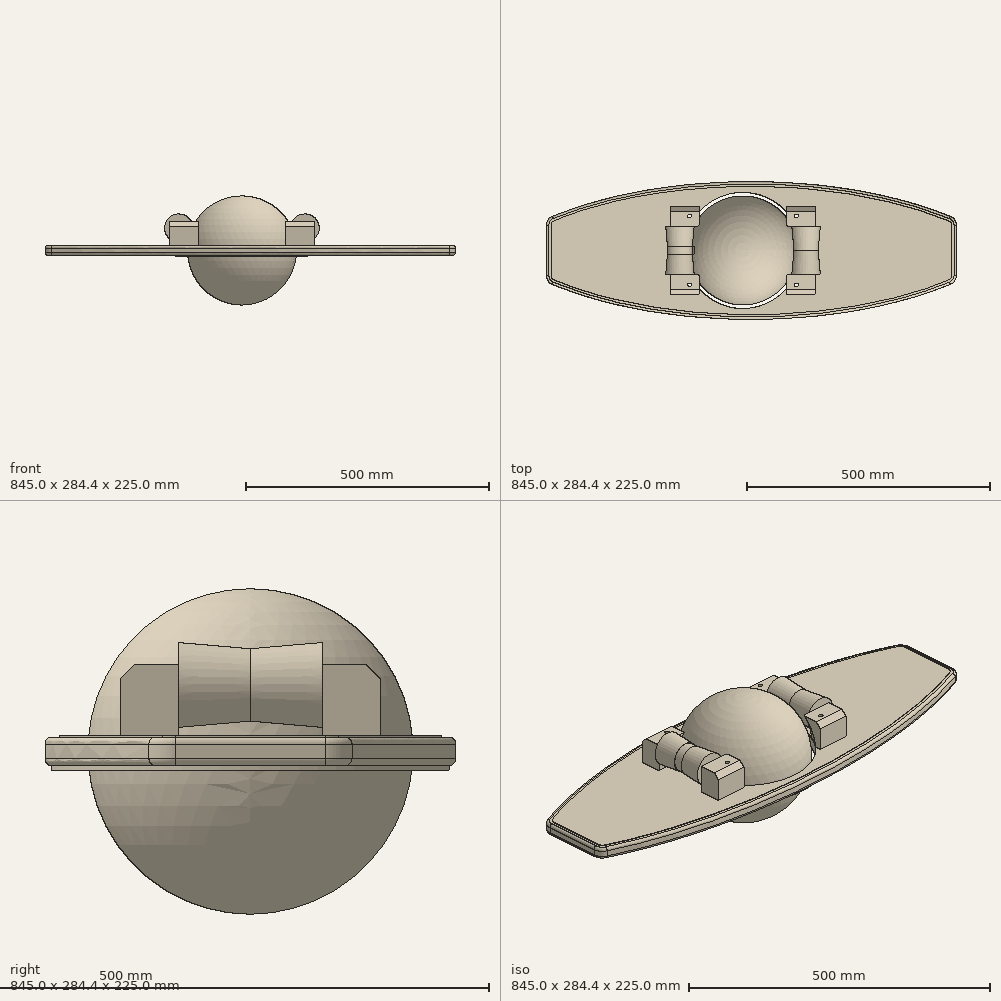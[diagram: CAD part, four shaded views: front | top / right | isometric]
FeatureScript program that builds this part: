
annotation { "Feature Type Name" : "Feature", "Feature Type Description" : "" }
export const myFeature = defineFeature(function(context is Context, id is Id, definition is map)
    precondition{}
    {
        {
            var Q0;
            Q0=qCreatedBy(makeId("Top.planeOp"),FACE);
            var sketch = newSketch(context, id + "F0", { "sketchPlane" : qUnion([Q0])});
            skLineSegment(sketch, "E0.bottom", {"start": v(440, 127.5) * mm, "end": v(-440, 127.5) * mm, "construction": true});
            skLineSegment(sketch, "E0.top", {"start": v(440, -127.5) * mm, "end": v(-440, -127.5) * mm, "construction": true});
            skLineSegment(sketch, "E0.left", {"start": v(440, 127.5) * mm, "end": v(440, -127.5) * mm, "construction": true});
            skLineSegment(sketch, "E0.right", {"start": v(-405, 51.76) * mm, "end": v(-405, -51.76) * mm});
            skPoint(sketch, "E0.middle", {"position": v(0, 0) * mm});
            skLineSegment(sketch, "E1", {"start": v(-441.65, 0) * mm, "end": v(552.98, 0) * mm, "construction": true});
            skPoint(sketch, "E1.startSnap0", {"position": v(-405, 0) * mm});
            skLineSegment(sketch, "E2", {"start": v(0, 265.18) * mm, "end": v(0, -302.26) * mm, "construction": true});
            skFitSpline(sketch, "E3", {"points": [v(-405, 65) * mm, v(440, 65) * mm], "startDerivative": vector(703.3, 306.5) * mm, "endDerivative": vector(719, -310.94) * mm});
            skFitSpline(sketch, "E4.MirrorCS", {"points": [v(-405, -65) * mm, v(440, -65) * mm], "startDerivative": vector(703.3, -306.5) * mm, "endDerivative": vector(719, 310.94) * mm});
            skLineSegment(sketch, "E5", {"start": v(440, -51.72) * mm, "end": v(440, 51.72) * mm});
            skPoint(sketch, "E6.newPointB", {"position": v(-405, 127.5) * mm});
            skArc(sketch, "E6.filletArc", {"start": v(-392.63, 70.25) * mm, "mid": v(-401.62, 62.88) * mm, "end": v(-405, 51.76) * mm});
            skPoint(sketch, "E7.newPointB", {"position": v(-405, -127.5) * mm});
            skArc(sketch, "E7.filletArc", {"start": v(-405, -51.76) * mm, "mid": v(-401.62, -62.88) * mm, "end": v(-392.63, -70.25) * mm});
            skArc(sketch, "E8.filletArc", {"start": v(440, 51.72) * mm, "mid": v(436.6, 62.86) * mm, "end": v(427.59, 70.23) * mm});
            skArc(sketch, "E9.filletArc", {"start": v(427.59, -70.23) * mm, "mid": v(436.6, -62.86) * mm, "end": v(440, -51.72) * mm});
            skSolve(sketch);
        }
        {
            var Q0;
            Q0 = qSketchRegion(id + "F0", true);
            extrude(context, id + "F1", {"entities" : qUnion([Q0]), "depth" : 10 * mm, "offsetDistance" : 25 * mm, "hasSecondDirection" : true, "secondDirectionOppositeDirection" : true, "secondDirectionDepth" : 10 * mm});
        }
        {
            var Q0;
            Q0=makeQuery(id+"F1.opExtrude","CAP_FACE",FACE,{"disambiguationData":[OSD([sQuery(id+"F0.wireOp",EDGE,"E0.right"),sQuery(id+"F0.wireOp",EDGE,"E3"),sQuery(id+"F0.wireOp",EDGE,"E4.MirrorCS"),sQuery(id+"F0.wireOp",EDGE,"E5"),sQuery(id+"F0.wireOp",EDGE,"E6.filletArc"),sQuery(id+"F0.wireOp",EDGE,"E7.filletArc"),sQuery(id+"F0.wireOp",EDGE,"E8.filletArc"),sQuery(id+"F0.wireOp",EDGE,"E9.filletArc")])],"isStart":false});
            var sketch = newSketch(context, id + "F2", { "sketchPlane" : qUnion([Q0])});
            skLineSegment(sketch, "E10", {"start": v(199.73, 164.42) * mm, "end": v(199.73, -153.38) * mm, "construction": true});
            skLineSegment(sketch, "E11.MirrorCS", {"start": v(-199.73, 164.42) * mm, "end": v(-199.73, -153.38) * mm, "construction": true});
            skEllipse(sketch, "E12", {"center": v(0, 0) * mm, "majorRadius": 262.5 * mm, "minorRadius": 137.5 * mm, "majorAxis": v(1, 0)});
            skSolve(sketch);
        }
        {
            var Q0;
            Q0=qCreatedBy(makeId("Front.planeOp"),FACE);
            var sketch = newSketch(context, id + "F3", { "sketchPlane" : qUnion([Q0])});
            skLineSegment(sketch, "E13", {"start": v(0, 153.53) * mm, "end": v(0, -137.68) * mm, "construction": true});
            skArc(sketch, "E14", {"start": v(0, -120) * mm, "mid": v(120, 0) * mm, "end": v(0, 120) * mm});
            skPoint(sketch, "E15", {"position": v(0, 120) * mm});
            skPoint(sketch, "E16", {"position": v(0, -120) * mm});
            skLineSegment(sketch, "E17", {"start": v(0, 120) * mm, "end": v(0, -120) * mm});
            skSolve(sketch);
        }
        {
            var Q0;
            Q0=makeQuery(id+"F1.opExtrude","CAP_FACE",FACE,{"disambiguationData":[OSD([sQuery(id+"F0.wireOp",EDGE,"E0.right"),sQuery(id+"F0.wireOp",EDGE,"E3"),sQuery(id+"F0.wireOp",EDGE,"E4.MirrorCS"),sQuery(id+"F0.wireOp",EDGE,"E5"),sQuery(id+"F0.wireOp",EDGE,"E6.filletArc"),sQuery(id+"F0.wireOp",EDGE,"E7.filletArc"),sQuery(id+"F0.wireOp",EDGE,"E8.filletArc"),sQuery(id+"F0.wireOp",EDGE,"E9.filletArc")])],"isStart":false});
            var sketch = newSketch(context, id + "F4", { "sketchPlane" : qUnion([Q0])});
            skCircle(sketch, "E18", {"center": v(0, 0) * mm, "radius": 120 * mm});
            skLineSegment(sketch, "E19", {"start": v(-413.94, 0) * mm, "end": v(421.24, 0) * mm, "construction": true});
            skPoint(sketch, "E19.endSnap0", {"position": v(-405, 0) * mm});
            skLineSegment(sketch, "E20", {"start": v(430.63, 50) * mm, "end": v(-484.6, 50) * mm, "construction": true});
            skLineSegment(sketch, "E21.bottom", {"start": v(180, 90) * mm, "end": v(90, 90) * mm});
            skLineSegment(sketch, "E21.top", {"start": v(180, 50) * mm, "end": v(90, 50) * mm});
            skLineSegment(sketch, "E21.left", {"start": v(180, 90) * mm, "end": v(180, 50) * mm});
            skLineSegment(sketch, "E21.right", {"start": v(90, 90) * mm, "end": v(90, 50) * mm});
            skLineSegment(sketch, "E22.MirrorCS", {"start": v(90, -90) * mm, "end": v(90, -50) * mm});
            skLineSegment(sketch, "E23.MirrorCS", {"start": v(180, -90) * mm, "end": v(90, -90) * mm});
            skLineSegment(sketch, "E24.MirrorCS", {"start": v(180, -90) * mm, "end": v(180, -50) * mm});
            skLineSegment(sketch, "E25.MirrorCS", {"start": v(180, -50) * mm, "end": v(90, -50) * mm});
            skLineSegment(sketch, "E26", {"start": v(0, 157.92) * mm, "end": v(0, -165.21) * mm, "construction": true});
            skLineSegment(sketch, "E27.MirrorCS", {"start": v(-90, -90) * mm, "end": v(-90, -50) * mm});
            skLineSegment(sketch, "E28.MirrorCS", {"start": v(-90, 90) * mm, "end": v(-90, 50) * mm});
            skLineSegment(sketch, "E29.MirrorCS", {"start": v(-180, 90) * mm, "end": v(-90, 90) * mm});
            skLineSegment(sketch, "E30.MirrorCS", {"start": v(-180, 90) * mm, "end": v(-180, 50) * mm});
            skLineSegment(sketch, "E31.MirrorCS", {"start": v(-180, -90) * mm, "end": v(-180, -50) * mm});
            skLineSegment(sketch, "E32.MirrorCS", {"start": v(-180, -90) * mm, "end": v(-90, -90) * mm});
            skLineSegment(sketch, "E33.MirrorCS", {"start": v(-180, -50) * mm, "end": v(-90, -50) * mm});
            skLineSegment(sketch, "E34.MirrorCS", {"start": v(-180, 50) * mm, "end": v(-90, 50) * mm});
            skSolve(sketch);
        }
        {
            var Q0;
            {var subQ4=sQuery(id+"F4.wireOp",EDGE,"E23.MirrorCS");Q0=makeQuery(id+"F4.imprint","IMPRINT",FACE,{"disambiguationData":[TD([[makeQuery(id+"F4.imprint","IMPRINT",EDGE,{"derivedFrom":subQ4}),-1.0]])]});}
            var Q1;
            {var subQ0=sQuery(id+"F4.wireOp",EDGE,"E25.MirrorCS");var subQ1=sQuery(id+"F4.wireOp",EDGE,"E22.MirrorCS");var subQ2=makeQuery(id+"F4.imprint","INTERSECT",VERTEX,{"derivedFrom":[subQ1,subQ0]});Q1=makeQuery(id+"F4.imprint","IMPRINT",FACE,{"disambiguationData":[TD([[makeQuery(id+"F4.imprint","IMPRINT",EDGE,{"disambiguationData":[TD([[subQ2,1.0]])],"derivedFrom":subQ1}),-1.0]])]});}
            extrude(context, id + "F5", {"entities" : qUnion([Q0, Q1]), "depth" : 50 * mm, "offsetDistance" : 25 * mm});
        }
        {
            var Q0;
            Q0 = qSketchRegion(id + "F3", true);
            var Q1;
            Q1=sQuery(id+"F3.wireOp",EDGE,"E13");
            revolve(context, id + "F6", {"operationType" : NewBodyOperationType.REMOVE, "entities" : qUnion([Q0]), "axis" : qUnion([Q1]), "revolveType" : RevolveType.FULL, "oppositeDirection" : true});
        }
        {
            var Q0;
            Q0=qCreatedBy(makeId("Front.planeOp"),FACE);
            var sketch = newSketch(context, id + "F7", { "sketchPlane" : qUnion([Q0])});
            skArc(sketch, "E35", {"start": v(0, -112.5) * mm, "mid": v(112.5, 0) * mm, "end": v(0, 112.5) * mm});
            skLineSegment(sketch, "E36", {"start": v(0, 156.26) * mm, "end": v(0, -184.84) * mm});
            skSolve(sketch);
        }
        {
            var Q0;
            Q0 = qSketchRegion(id + "F7", true);
            var Q1;
            Q1=sQuery(id+"F7.wireOp",EDGE,"E36");
            revolve(context, id + "F8", {"entities" : qUnion([Q0]), "axis" : qUnion([Q1]), "revolveType" : RevolveType.FULL});
        }
        {
            var Q0;
            Q0=qCreatedBy(makeId("Front.planeOp"),FACE);
            var sketch = newSketch(context, id + "F9", { "sketchPlane" : qUnion([Q0])});
            skCircle(sketch, "E37", {"center": v(130, 46) * mm, "radius": 25 * mm});
            skCircle(sketch, "E38", {"center": v(130, 46) * mm, "radius": 6 * mm});
            skSolve(sketch);
        }
        {
            var Q0;
            Q0=makeQuery(id+"F5.opExtrude","SWEPT_FACE",FACE,{"disambiguationData":[OSD([sQuery(id+"F4.wireOp",EDGE,"E25.MirrorCS")])]});
            var sketch = newSketch(context, id + "F10", { "sketchPlane" : qUnion([Q0])});
            skCircle(sketch, "E39.0", {"center": v(-130, 46) * mm, "radius": 6 * mm});
            skSolve(sketch);
        }
        {
            var Q0;
            Q0 = qSketchRegion(id + "F10", true);
            extrude(context, id + "F11", {"entities" : qUnion([Q0]), "operationType" : NewBodyOperationType.REMOVE, "oppositeDirection" : true, "depth" : 20 * mm, "offsetDistance" : 25 * mm});
        }
        {
            var Q0;
            Q0=makeQuery(id+"F5.opExtrude","SWEPT_FACE",FACE,{"disambiguationData":[OSD([sQuery(id+"F4.wireOp",EDGE,"E25.MirrorCS")])]});
            var sketch = newSketch(context, id + "F12", { "sketchPlane" : qUnion([Q0])});
            skLineSegment(sketch, "E40.bottom", {"start": v(-180, 60) * mm, "end": v(-150, 60) * mm});
            skLineSegment(sketch, "E40.top", {"start": v(-180, 10) * mm, "end": v(-150, 10) * mm});
            skLineSegment(sketch, "E40.left", {"start": v(-180, 60) * mm, "end": v(-180, 10) * mm});
            skLineSegment(sketch, "E40.right", {"start": v(-150, 60) * mm, "end": v(-150, 10) * mm});
            skSolve(sketch);
        }
        {
            var Q0;
            Q0 = qSketchRegion(id + "F12", true);
            extrude(context, id + "F13", {"entities" : qUnion([Q0]), "operationType" : NewBodyOperationType.REMOVE, "endBound" : BoundingType.THROUGH_ALL, "oppositeDirection" : true, "depth" : 25 * mm, "offsetDistance" : 25 * mm});
        }
        {
            var Q0;
            Q0=makeQuery(id+"F9.imprint","IMPRINT",FACE,{"disambiguationData":[TD([[makeQuery(id+"F9.imprint","IMPRINT",EDGE,{"derivedFrom":sQuery(id+"F9.wireOp",EDGE,"E37")}),1.0]])]});
            extrude(context, id + "F14", {"entities" : qUnion([Q0]), "depth" : 49.5 * mm, "offsetDistance" : 25 * mm, "hasDraft" : true, "draftAngle" : 5 * degree, "hasSecondDirection" : true, "secondDirectionOppositeDirection" : true, "secondDirectionDepth" : 49.5 * mm, "hasSecondDirectionDraft" : true, "secondDirectionDraftAngle" : 5 * degree});
        }
        {
            var Q0;
            Q0=makeQuery(id+"F14.opExtrude","CAP_FACE",FACE,{"disambiguationData":[OSD([sQuery(id+"F9.wireOp",EDGE,"E37"),sQuery(id+"F9.wireOp",EDGE,"E38")])],"isStart":true});
            var sketch = newSketch(context, id + "F15", { "sketchPlane" : qUnion([Q0])});
            skCircle(sketch, "E41", {"center": v(-130, 46) * mm, "radius": 6 * mm});
            skSolve(sketch);
        }
        {
            var Q0;
            Q0 = qSketchRegion(id + "F15", true);
            var Q1;
            Q1=makeQuery(id+"F14.opExtrude","CAP_FACE",FACE,{"disambiguationData":[OSD([sQuery(id+"F9.wireOp",EDGE,"E37"),sQuery(id+"F9.wireOp",EDGE,"E38")])],"isStart":false});
            extrude(context, id + "F16", {"entities" : qUnion([Q0]), "operationType" : NewBodyOperationType.REMOVE, "endBound" : BoundingType.UP_TO_SURFACE, "oppositeDirection" : true, "depth" : 25 * mm, "endBoundEntityFace" : qUnion([Q1]), "offsetDistance" : 25 * mm});
        }
        {
            var Q0;
            Q0=qCreatedBy(makeId("Front.planeOp"),FACE);
            var sketch = newSketch(context, id + "F17", { "sketchPlane" : qUnion([Q0])});
            skCircle(sketch, "E42.0", {"center": v(130, 46) * mm, "radius": 6 * mm});
            skSolve(sketch);
        }
        {
            var Q0;
            Q0=makeQuery(id+"F5.opExtrude","CAP_FACE",FACE,{"disambiguationData":[OSD([sQuery(id+"F4.wireOp",EDGE,"E22.MirrorCS"),sQuery(id+"F4.wireOp",EDGE,"E23.MirrorCS"),sQuery(id+"F4.wireOp",EDGE,"E24.MirrorCS"),sQuery(id+"F4.wireOp",EDGE,"E25.MirrorCS")])],"isStart":false});
            var sketch = newSketch(context, id + "F18", { "sketchPlane" : qUnion([Q0])});
            skCircle(sketch, "E43", {"center": v(110, -70.98) * mm, "radius": 4 * mm});
            skPoint(sketch, "E43.centerSnap0", {"position": v(90, -70.98) * mm});
            skSolve(sketch);
        }
        {
            var Q0;
            Q0=makeQuery(id+"F18.imprint","IMPRINT",FACE,{"disambiguationData":[TD([[makeQuery(id+"F18.imprint","IMPRINT",EDGE,{"derivedFrom":sQuery(id+"F18.wireOp",EDGE,"E43")}),1.0]])]});
            extrude(context, id + "F19", {"entities" : qUnion([Q0]), "operationType" : NewBodyOperationType.REMOVE, "endBound" : BoundingType.THROUGH_ALL, "oppositeDirection" : true, "depth" : 25 * mm, "offsetDistance" : 25 * mm});
        }
        {
            var Q0;
            Q0=makeQuery(id+"F5.opExtrude","SWEPT_EDGE",EDGE,{"disambiguationData":[OSD([sQuery(id+"F4.wireOp",EDGE,"E23.MirrorCS"),sQuery(id+"F4.wireOp",EDGE,"E24.MirrorCS")])]});
            var Q1;
            Q1=makeQuery(id+"F5.opExtrude","CAP_EDGE",EDGE,{"disambiguationData":[OSD([sQuery(id+"F4.wireOp",EDGE,"E23.MirrorCS")])],"isStart":false});
            chamfer(context, id + "F20", {"entities" : qUnion([Q0, Q1]), "width" : 10 * mm, "tangentPropagation" : true});
        }
        {
            var Q0;
            Q0=makeQuery(id+"F5.opExtrude","SWEPT_BODY",BODY,{"disambiguationData":[OSD([sQuery(id+"F4.wireOp",EDGE,"E22.MirrorCS"),sQuery(id+"F4.wireOp",EDGE,"E23.MirrorCS"),sQuery(id+"F4.wireOp",EDGE,"E24.MirrorCS"),sQuery(id+"F4.wireOp",EDGE,"E25.MirrorCS")])]});
            var Q1;
            Q1=qCreatedBy(makeId("Front.planeOp"),FACE);
            mirror(context, id + "F21", {"entities" : qUnion([Q0]), "mirrorPlane" : qUnion([Q1])});
        }
        {
            var Q0;
            Q0=makeQuery(id+"F5.opExtrude","SWEPT_BODY",BODY,{"disambiguationData":[OSD([sQuery(id+"F4.wireOp",EDGE,"E22.MirrorCS"),sQuery(id+"F4.wireOp",EDGE,"E23.MirrorCS"),sQuery(id+"F4.wireOp",EDGE,"E24.MirrorCS"),sQuery(id+"F4.wireOp",EDGE,"E25.MirrorCS")])]});
            var Q1;
            Q1=makeQuery(id+"F14.*.split.splitOp","SPLIT",BODY,{"derivedFrom":makeQuery(id+"F14.opExtrude","SWEPT_BODY",BODY,{"disambiguationData":[OSD([sQuery(id+"F9.wireOp",EDGE,"E37"),sQuery(id+"F9.wireOp",EDGE,"E38")])]})});
            var Q2;
            Q2=makeQuery(id+"F21.opPattern","COPY",BODY,{"derivedFrom":makeQuery(id+"F5.opExtrude","SWEPT_BODY",BODY,{"disambiguationData":[OSD([sQuery(id+"F4.wireOp",EDGE,"E22.MirrorCS"),sQuery(id+"F4.wireOp",EDGE,"E23.MirrorCS"),sQuery(id+"F4.wireOp",EDGE,"E24.MirrorCS"),sQuery(id+"F4.wireOp",EDGE,"E25.MirrorCS")])]}),"instanceName":"1"});
            var Q3;
            Q3=makeQuery(id+"FzdrouotUrJtnVR_6.opExtrude","SWEPT_BODY",BODY,{"disambiguationData":[OSD([sQuery(id+"F17.wireOp",EDGE,"E42.0")])]});
            var Q4;
            Q4=qCreatedBy(makeId("Right.planeOp"),FACE);
            mirror(context, id + "F22", {"entities" : qUnion([Q0, Q1, Q2, Q3]), "mirrorPlane" : qUnion([Q4])});
        }
        {
            var Q0;
            Q0=makeQuery(id+"F1.opExtrude","CAP_FACE",FACE,{"disambiguationData":[OSD([sQuery(id+"F0.wireOp",EDGE,"E0.right"),sQuery(id+"F0.wireOp",EDGE,"E3"),sQuery(id+"F0.wireOp",EDGE,"E4.MirrorCS"),sQuery(id+"F0.wireOp",EDGE,"E5"),sQuery(id+"F0.wireOp",EDGE,"E6.filletArc"),sQuery(id+"F0.wireOp",EDGE,"E7.filletArc"),sQuery(id+"F0.wireOp",EDGE,"E8.filletArc"),sQuery(id+"F0.wireOp",EDGE,"E9.filletArc")])],"isStart":true});
            var sketch = newSketch(context, id + "F23", { "sketchPlane" : qUnion([Q0])});
            skSolve(sketch);
        }
        {
            var Q0;
            Q0=makeQuery(id+"F2.imprint","IMPRINT",FACE,{"disambiguationData":[TD([[makeQuery(id+"F2.imprint","IMPRINT",EDGE,{"derivedFrom":sQuery(id+"F2.wireOp",EDGE,"E12")}),-1.0]])]});
            cPlane(context, id + "F24", {"entities" : qUnion([Q0]), "cplaneType" : CPlaneType.OFFSET, "offset" : 80 * mm, "width" : 150 * mm, "height" : 150 * mm});
        }
        {
            var Q0;
            Q0=makeQuery(id+"F1.opExtrude","CAP_EDGE",EDGE,{"disambiguationData":[OSD([sQuery(id+"F0.wireOp",EDGE,"E3")])],"isStart":false});
            var Q1;
            Q1=makeQuery(id+"F1.opExtrude","CAP_EDGE",EDGE,{"disambiguationData":[OSD([sQuery(id+"F0.wireOp",EDGE,"E3")])],"isStart":true});
            fillet(context, id + "F25", {"entities" : qUnion([Q0, Q1]), "radius" : 5 * mm, "tangentPropagation" : true, "allowEdgeOverflow" : false});
        }
        {
            var Q0;
            Q0=makeQuery(id+"F2.imprint","IMPRINT",FACE,{"disambiguationData":[TD([[makeQuery(id+"F2.imprint","IMPRINT",EDGE,{"derivedFrom":sQuery(id+"F2.wireOp",EDGE,"E12")}),-1.0]])]});
            cPlane(context, id + "F26", {"entities" : qUnion([Q0]), "cplaneType" : CPlaneType.OFFSET, "offset" : 58 * mm, "width" : 150 * mm, "height" : 150 * mm});
        }
        {
            var Q0;
            Q0=qCreatedBy(makeId("Front.planeOp"),FACE);
            var sketch = newSketch(context, id + "F27", { "sketchPlane" : qUnion([Q0])});
            skCircle(sketch, "E44.0", {"center": v(-130, 46) * mm, "radius": 25 * mm});
            skCircle(sketch, "E45.0", {"center": v(-130, 46) * mm, "radius": 29.33 * mm});
            skSolve(sketch);
        }
        {
            var Q0;
            Q0 = qSketchRegion(id + "F27", true);
            extrude(context, id + "F28", {"entities" : qUnion([Q0]), "operationType" : NewBodyOperationType.REMOVE, "oppositeDirection" : true, "depth" : 8 * mm, "offsetDistance" : 25 * mm, "hasSecondDirection" : true, "secondDirectionOppositeDirection" : false, "secondDirectionDepth" : 8 * mm});
        }
        {
            var Q0;
            Q0=makeQuery(id+"F21.opPattern","COPY",FACE,{"derivedFrom":makeQuery(id+"F11.boolean.opBoolean","COPY",FACE,{"derivedFrom":makeQuery(id+"F11.opExtrude","CAP_FACE",FACE,{"disambiguationData":[OSD([sQuery(id+"F10.wireOp",EDGE,"E39.0")])],"isStart":false})}),"instanceName":"1"});
            var sketch = newSketch(context, id + "F29", { "sketchPlane" : qUnion([Q0])});
            skCircle(sketch, "E46.0", {"center": v(130, 46) * mm, "radius": 6 * mm});
            skSolve(sketch);
        }
        {
            var Q0;
            Q0 = qSketchRegion(id + "F29", true);
            var Q1;
            Q1=makeQuery(id+"F11.boolean.opBoolean","COPY",FACE,{"derivedFrom":makeQuery(id+"F11.opExtrude","CAP_FACE",FACE,{"disambiguationData":[OSD([sQuery(id+"F10.wireOp",EDGE,"E39.0")])],"isStart":false})});
            extrude(context, id + "F30", {"entities" : qUnion([Q0]), "endBound" : BoundingType.UP_TO_SURFACE, "depth" : 25 * mm, "endBoundEntityFace" : qUnion([Q1]), "offsetDistance" : 25 * mm});
        }
        {
            var Q0;
            Q0=makeQuery(id+"F30.opExtrude","SWEPT_BODY",BODY,{"disambiguationData":[OSD([sQuery(id+"F29.wireOp",EDGE,"E46.0")])]});
            var Q1;
            Q1=qCreatedBy(makeId("Right.planeOp"),FACE);
            mirror(context, id + "F31", {"entities" : qUnion([Q0]), "mirrorPlane" : qUnion([Q1])});
        }
        {
            var Q0;
            {var subQ3=sQuery(id+"F0.wireOp",EDGE,"E0.right");Q0=makeQuery(id+"F23.imprint","IMPRINT",FACE,{"disambiguationData":[TD([[makeQuery(id+"F23.imprint","IMPRINT",EDGE,{"derivedFrom":makeQuery(id+"F1.opExtrude","CAP_EDGE",EDGE,{"disambiguationData":[OSD([subQ3])],"isStart":true})}),-1.0]])]});}
            var sketch = newSketch(context, id + "F32", { "sketchPlane" : qUnion([Q0])});
            skCircle(sketch, "E47.0", {"center": v(110, 70.98) * mm, "radius": 4 * mm});
            skCircle(sketch, "E48.0", {"center": v(-110, 70.98) * mm, "radius": 4 * mm});
            skCircle(sketch, "E49.0", {"center": v(-110, -70.98) * mm, "radius": 4 * mm});
            skCircle(sketch, "E50.0", {"center": v(110, -70.98) * mm, "radius": 4 * mm});
            skSolve(sketch);
        }
        {
            var Q0;
            Q0 = qSketchRegion(id + "F32", true);
            extrude(context, id + "F33", {"entities" : qUnion([Q0]), "operationType" : NewBodyOperationType.REMOVE, "endBound" : BoundingType.THROUGH_ALL, "oppositeDirection" : true, "depth" : 25 * mm, "offsetDistance" : 25 * mm});
        }
        {
            var Q0;
            Q0=makeQuery(id+"F1.opExtrude","CAP_FACE",FACE,{"disambiguationData":[OSD([sQuery(id+"F0.wireOp",EDGE,"E0.right"),sQuery(id+"F0.wireOp",EDGE,"E3"),sQuery(id+"F0.wireOp",EDGE,"E4.MirrorCS"),sQuery(id+"F0.wireOp",EDGE,"E5"),sQuery(id+"F0.wireOp",EDGE,"E6.filletArc"),sQuery(id+"F0.wireOp",EDGE,"E7.filletArc"),sQuery(id+"F0.wireOp",EDGE,"E8.filletArc"),sQuery(id+"F0.wireOp",EDGE,"E9.filletArc")])],"isStart":true});
            var sketch = newSketch(context, id + "F34", { "sketchPlane" : qUnion([Q0])});
            skCircle(sketch, "E51.0", {"center": v(0, 0) * mm, "radius": 122.58 * mm});
            skCircle(sketch, "E52.0", {"center": v(0, 0) * mm, "radius": 137.58 * mm});
            skCircle(sketch, "E53.0", {"center": v(-110, 70.98) * mm, "radius": 4 * mm});
            skCircle(sketch, "E54.0", {"center": v(110, 70.98) * mm, "radius": 4 * mm});
            skCircle(sketch, "E55.0", {"center": v(110, -70.98) * mm, "radius": 4 * mm});
            skCircle(sketch, "E56.0", {"center": v(-110, -70.98) * mm, "radius": 4 * mm});
            skSolve(sketch);
        }
        {
            var Q0;
            Q0 = qSketchRegion(id + "F34", true);
            extrude(context, id + "F35", {"entities" : qUnion([Q0]), "depth" : 3 * mm, "offsetDistance" : 25 * mm});
        }
        {
            var Q0;
            Q0=makeQuery(id+"F31.opPattern","COPY",FACE,{"derivedFrom":makeQuery(id+"F30.opExtrude","CAP_FACE",FACE,{"disambiguationData":[OSD([sQuery(id+"F29.wireOp",EDGE,"E46.0")])],"isStart":false}),"instanceName":"1"});
            var sketch = newSketch(context, id + "F36", { "sketchPlane" : qUnion([Q0])});
            skCircle(sketch, "E57.0", {"center": v(-130, 46) * mm, "radius": 6 * mm});
            skSolve(sketch);
        }
        {
            var Q0;
            Q0 = qSketchRegion(id + "F36", true);
            extrude(context, id + "F37", {"entities" : qUnion([Q0]), "operationType" : NewBodyOperationType.REMOVE, "oppositeDirection" : true, "depth" : 20 * mm, "offsetDistance" : 25 * mm});
        }
        {
            var Q0;
            Q0=makeQuery(id+"F37.boolean.opBoolean","COPY",FACE,{"derivedFrom":makeQuery(id+"F37.opExtrude","CAP_FACE",FACE,{"disambiguationData":[OSD([sQuery(id+"F36.wireOp",EDGE,"E57.0")])],"isStart":false})});
            var sketch = newSketch(context, id + "F38", { "sketchPlane" : qUnion([Q0])});
            skCircle(sketch, "E58", {"center": v(-130, 46) * mm, "radius": 2.5 * mm});
            skSolve(sketch);
        }
        {
            var Q0;
            Q0 = qSketchRegion(id + "F38", true);
            extrude(context, id + "F39", {"entities" : qUnion([Q0]), "operationType" : NewBodyOperationType.REMOVE, "oppositeDirection" : true, "depth" : 25 * mm, "offsetDistance" : 25 * mm});
        }
        {
            var Q0;
            Q0=makeQuery(id+"F1.opExtrude","CAP_FACE",FACE,{"disambiguationData":[OSD([sQuery(id+"F0.wireOp",EDGE,"E0.right"),sQuery(id+"F0.wireOp",EDGE,"E3"),sQuery(id+"F0.wireOp",EDGE,"E4.MirrorCS"),sQuery(id+"F0.wireOp",EDGE,"E5"),sQuery(id+"F0.wireOp",EDGE,"E6.filletArc"),sQuery(id+"F0.wireOp",EDGE,"E7.filletArc"),sQuery(id+"F0.wireOp",EDGE,"E8.filletArc"),sQuery(id+"F0.wireOp",EDGE,"E9.filletArc")])],"isStart":false});
            var sketch = newSketch(context, id + "F40", { "sketchPlane" : qUnion([Q0])});
            skLineSegment(sketch, "E59.0", {"start": v(-395, 51.76) * mm, "end": v(-395, -51.76) * mm});
            skArc(sketch, "E59.1", {"start": v(-388.81, 61) * mm, "mid": v(-393.31, 57.32) * mm, "end": v(-395, 51.76) * mm});
            skArc(sketch, "E59.2", {"start": v(-395, -51.76) * mm, "mid": v(-393.31, -57.32) * mm, "end": v(-388.81, -61) * mm});
            skFitSpline(sketch, "E59.3", {"points": [v(423.8, 60.97) * mm, v(415.73, 64.28) * mm, v(399.5, 70.59) * mm, v(374.86, 79.2) * mm, v(354.1, 85.75) * mm, v(337.37, 90.62) * mm, v(326.86, 93.51) * mm, v(318.43, 95.74) * mm, v(309.99, 97.91) * mm, v(299.43, 100.52) * mm, v(286.75, 103.47) * mm, v(269.82, 107.18) * mm, v(248.63, 111.42) * mm, v(223.15, 115.9) * mm, v(197.62, 119.8) * mm, v(163.53, 124.25) * mm, v(120.82, 128.48) * mm, v(69.4, 131.5) * mm, v(26.44, 132.34) * mm, v(-8, 132.03) * mm, v(-33.86, 131.29) * mm, v(-59.77, 130.04) * mm, v(-81.38, 128.57) * mm, v(-98.69, 127.13) * mm, v(-109.51, 126.12) * mm, v(-118.18, 125.24) * mm, v(-126.83, 124.32) * mm, v(-137.63, 123.08) * mm, v(-150.55, 121.46) * mm, v(-167.74, 119.12) * mm, v(-197.7, 114.53) * mm, v(-240.15, 106.55) * mm, v(-290.49, 94.5) * mm, v(-340.13, 79.67) * mm, v(-372.7, 67.65) * mm, v(-388.81, 61) * mm]});
            skFitSpline(sketch, "E59.4", {"points": [v(-388.81, -61) * mm, v(-380.76, -64.33) * mm, v(-364.54, -70.66) * mm, v(-339.91, -79.31) * mm, v(-319.16, -85.86) * mm, v(-302.43, -90.73) * mm, v(-291.92, -93.63) * mm, v(-283.49, -95.86) * mm, v(-275.05, -98.03) * mm, v(-264.5, -100.63) * mm, v(-251.8, -103.58) * mm, v(-234.88, -107.3) * mm, v(-213.69, -111.52) * mm, v(-188.2, -116) * mm, v(-162.68, -119.88) * mm, v(-128.59, -124.32) * mm, v(-85.87, -128.52) * mm, v(-34.46, -131.52) * mm, v(8.5, -132.35) * mm, v(42.94, -132.02) * mm, v(68.8, -131.27) * mm, v(94.7, -130) * mm, v(116.32, -128.53) * mm, v(133.62, -127.08) * mm, v(144.45, -126.06) * mm, v(153.11, -125.18) * mm, v(161.77, -124.25) * mm, v(172.56, -123.01) * mm, v(185.49, -121.38) * mm, v(202.67, -119.03) * mm, v(232.63, -114.43) * mm, v(275.09, -106.44) * mm, v(325.42, -94.37) * mm, v(375.08, -79.56) * mm, v(407.66, -67.59) * mm, v(423.8, -60.97) * mm]});
            skArc(sketch, "E59.5", {"start": v(423.8, -60.97) * mm, "mid": v(428.3, -57.3) * mm, "end": v(430, -51.72) * mm});
            skLineSegment(sketch, "E59.6", {"start": v(430, -51.72) * mm, "end": v(430, 51.72) * mm});
            skArc(sketch, "E59.7", {"start": v(430, 51.72) * mm, "mid": v(428.3, 57.3) * mm, "end": v(423.8, 60.97) * mm});
            skLineSegment(sketch, "E60", {"start": v(-195, 148.69) * mm, "end": v(-195, -154.62) * mm, "construction": true});
            skLineSegment(sketch, "E61", {"start": v(49.68, 0) * mm, "end": v(-514.02, 0) * mm, "construction": true});
            skFitSpline(sketch, "E62", {"points": [v(-195, 114.76) * mm, v(-195, -114.76) * mm], "startDerivative": vector(-210, -254.28) * mm, "endDerivative": vector(210, -254.28) * mm});
            skLineSegment(sketch, "E63.0", {"start": v(-265, 148.69) * mm, "end": v(-265, -154.62) * mm});
            skLineSegment(sketch, "E64.0", {"start": v(49.68, 30) * mm, "end": v(-514.02, 30) * mm, "construction": true});
            skLineSegment(sketch, "E65.0", {"start": v(49.68, -30) * mm, "end": v(-514.02, -30) * mm, "construction": true});
            skSolve(sketch);
        }
        {
            var Q0;
            Q0=makeQuery(id+"F40.imprint","IMPRINT",FACE,{"disambiguationData":[TD([[makeQuery(id+"F40.imprint","IMPRINT",EDGE,{"derivedFrom":sQuery(id+"F40.wireOp",EDGE,"E59.0")}),1.0]])]});
            var Q1;
            {var subQ0=sQuery(id+"F40.wireOp",EDGE,"E62");Q1=makeQuery(id+"F40.imprint","IMPRINT",FACE,{"disambiguationData":[TD([[makeQuery(id+"F40.imprint","IMPRINT",EDGE,{"derivedFrom":subQ0}),-1.0]])]});}
            extrude(context, id + "F41", {"entities" : qUnion([Q0, Q1]), "operationType" : NewBodyOperationType.REMOVE, "oppositeDirection" : true, "depth" : 2 * mm, "offsetDistance" : 25 * mm});
        }
        {
            var Q0;
            Q0=makeQuery(id+"F1.opExtrude","CAP_FACE",FACE,{"disambiguationData":[OSD([sQuery(id+"F0.wireOp",EDGE,"E0.right"),sQuery(id+"F0.wireOp",EDGE,"E3"),sQuery(id+"F0.wireOp",EDGE,"E4.MirrorCS"),sQuery(id+"F0.wireOp",EDGE,"E5"),sQuery(id+"F0.wireOp",EDGE,"E6.filletArc"),sQuery(id+"F0.wireOp",EDGE,"E7.filletArc"),sQuery(id+"F0.wireOp",EDGE,"E8.filletArc"),sQuery(id+"F0.wireOp",EDGE,"E9.filletArc")])],"isStart":false});
            var sketch = newSketch(context, id + "F42", { "sketchPlane" : qUnion([Q0])});
            skLineSegment(sketch, "E66.0", {"start": v(-395, 51.76) * mm, "end": v(-395, -51.76) * mm});
            skArc(sketch, "E66.1", {"start": v(-388.81, 61) * mm, "mid": v(-393.31, 57.32) * mm, "end": v(-395, 51.76) * mm});
            skArc(sketch, "E66.2", {"start": v(-395, -51.76) * mm, "mid": v(-393.31, -57.32) * mm, "end": v(-388.81, -61) * mm});
            skFitSpline(sketch, "E66.3", {"points": [v(423.8, 60.97) * mm, v(415.73, 64.28) * mm, v(399.5, 70.59) * mm, v(374.86, 79.2) * mm, v(354.1, 85.75) * mm, v(337.37, 90.62) * mm, v(326.86, 93.51) * mm, v(318.43, 95.74) * mm, v(309.99, 97.91) * mm, v(299.43, 100.52) * mm, v(286.75, 103.47) * mm, v(269.82, 107.18) * mm, v(248.63, 111.42) * mm, v(223.15, 115.9) * mm, v(197.62, 119.8) * mm, v(163.53, 124.25) * mm, v(120.82, 128.48) * mm, v(69.4, 131.5) * mm, v(26.44, 132.34) * mm, v(-8, 132.03) * mm, v(-33.86, 131.29) * mm, v(-59.77, 130.04) * mm, v(-81.38, 128.57) * mm, v(-98.69, 127.13) * mm, v(-109.51, 126.12) * mm, v(-118.18, 125.24) * mm, v(-126.83, 124.32) * mm, v(-137.63, 123.08) * mm, v(-150.55, 121.46) * mm, v(-167.74, 119.12) * mm, v(-197.7, 114.53) * mm, v(-240.15, 106.55) * mm, v(-290.49, 94.5) * mm, v(-340.13, 79.67) * mm, v(-372.7, 67.65) * mm, v(-388.81, 61) * mm]});
            skFitSpline(sketch, "E66.4", {"points": [v(-388.81, -61) * mm, v(-380.76, -64.33) * mm, v(-364.54, -70.66) * mm, v(-339.91, -79.31) * mm, v(-319.16, -85.86) * mm, v(-302.43, -90.73) * mm, v(-291.92, -93.63) * mm, v(-283.49, -95.86) * mm, v(-275.05, -98.03) * mm, v(-264.5, -100.63) * mm, v(-251.8, -103.58) * mm, v(-234.88, -107.3) * mm, v(-213.69, -111.52) * mm, v(-188.2, -116) * mm, v(-162.68, -119.88) * mm, v(-128.59, -124.32) * mm, v(-85.87, -128.52) * mm, v(-34.46, -131.52) * mm, v(8.5, -132.35) * mm, v(42.94, -132.02) * mm, v(68.8, -131.27) * mm, v(94.7, -130) * mm, v(116.32, -128.53) * mm, v(133.62, -127.08) * mm, v(144.45, -126.06) * mm, v(153.11, -125.18) * mm, v(161.77, -124.25) * mm, v(172.56, -123.01) * mm, v(185.49, -121.38) * mm, v(202.67, -119.03) * mm, v(232.63, -114.43) * mm, v(275.09, -106.44) * mm, v(325.42, -94.37) * mm, v(375.08, -79.56) * mm, v(407.66, -67.59) * mm, v(423.8, -60.97) * mm]});
            skArc(sketch, "E66.5", {"start": v(423.8, -60.97) * mm, "mid": v(428.3, -57.3) * mm, "end": v(430, -51.72) * mm});
            skLineSegment(sketch, "E66.6", {"start": v(430, -51.72) * mm, "end": v(430, 51.72) * mm});
            skArc(sketch, "E66.7", {"start": v(430, 51.72) * mm, "mid": v(428.3, 57.3) * mm, "end": v(423.8, 60.97) * mm});
            skLineSegment(sketch, "E67", {"start": v(538.57, 0) * mm, "end": v(-76.36, 0) * mm, "construction": true});
            skLineSegment(sketch, "E68", {"start": v(175, 192.9) * mm, "end": v(175, -230.44) * mm, "construction": true});
            skLineSegment(sketch, "E69", {"start": v(265, -213.6) * mm, "end": v(265, 239.5) * mm, "construction": true});
            skLineSegment(sketch, "E70", {"start": v(523.04, 30) * mm, "end": v(-33.64, 30) * mm, "construction": true});
            skLineSegment(sketch, "E71", {"start": v(-34.93, -30) * mm, "end": v(564.93, -30) * mm, "construction": true});
            skFitSpline(sketch, "E72", {"points": [v(175, 122.7) * mm, v(175, -122.7) * mm], "startDerivative": vector(270, -278.08) * mm, "endDerivative": vector(-270, -278.08) * mm});
            skPoint(sketch, "E73", {"position": v(231.1, 0) * mm});
            skSolve(sketch);
        }
        {
            var Q0;
            {var subQ0=sQuery(id+"F42.wireOp",EDGE,"E66.5");Q0=makeQuery(id+"F42.imprint","IMPRINT",FACE,{"disambiguationData":[TD([[makeQuery(id+"F42.imprint","IMPRINT",EDGE,{"derivedFrom":subQ0}),1.0]])]});}
            extrude(context, id + "F43", {"entities" : qUnion([Q0]), "operationType" : NewBodyOperationType.REMOVE, "oppositeDirection" : true, "depth" : 2 * mm, "offsetDistance" : 25 * mm});
        }
        {
            var Q0;
            Q0=makeQuery(id+"F41.boolean.opBoolean","COPY",FACE,{"derivedFrom":makeQuery(id+"F41.opExtrude","CAP_FACE",FACE,{"disambiguationData":[OSD([sQuery(id+"F40.wireOp",EDGE,"E59.0"),sQuery(id+"F40.wireOp",EDGE,"E59.1"),sQuery(id+"F40.wireOp",EDGE,"E59.2"),sQuery(id+"F40.wireOp",EDGE,"E59.3"),sQuery(id+"F40.wireOp",EDGE,"E59.4"),sQuery(id+"F40.wireOp",EDGE,"E62")])],"isStart":false})});
            var Q1;
            Q1=makeQuery(id+"F43.boolean.opBoolean","COPY",FACE,{"derivedFrom":makeQuery(id+"F43.opExtrude","CAP_FACE",FACE,{"disambiguationData":[OSD([sQuery(id+"F42.wireOp",EDGE,"E66.3"),sQuery(id+"F42.wireOp",EDGE,"E66.4"),sQuery(id+"F42.wireOp",EDGE,"E66.5"),sQuery(id+"F42.wireOp",EDGE,"E66.6"),sQuery(id+"F42.wireOp",EDGE,"E66.7"),sQuery(id+"F42.wireOp",EDGE,"E72")])],"isStart":false})});
            extrude(context, id + "F44", {"entities" : qUnion([Q0, Q1]), "depth" : 3 * mm, "offsetDistance" : 25 * mm});
        }
    });
